# Revit family: Studio-8-Window-1
name_source: partatom
category: Windows
units: mm (PartAtom-declared; Revit-internal decimal feet)

## family parameters
Always vertical = Yes
Cut with Voids When Loaded = No
Host = Wall
OmniClass Number = 23.30.20.00
OmniClass Title = Windows
Room Calculation Point = No
Shared = No

## types (4) — shared parameters
Analytic Construction = <None>
Assembly Code = C1030
Default Sill Height = 2' - 7 1/2"
Define Thermal Properties by = Schematic Type
Description = Soundproof interior windows
Frame Finish = Clear / Dark Bronze Anodized
Frame Material = Aluminum – Studio (4/5/6/8) Soundproof Window
Glass = Laminated Glass – Studio (4/5/6/8) Soundproof Window
Height = 3' - 0"
Manufacturer = Acoustical Surfaces, Inc.
Rough Height = 3' - 0 1/2"
Type Comments = Soundproof windows
URL = https://www.acousticalsurfaces.com
Wall Closure = By host

## per-type parameters (varying)
| type | Angled | Flat | Rough Width | Width | a |
| FLAT 48 x 36 | No | Yes | 4' - 0 1/2" | 4' - 0" | 3' - 8 1/2" |
| FLAT 72 x 36 | No | Yes | 6' - 0 1/2" | 6' - 0" | 5' - 8 1/2" |
| ANGLED 72 x 36 | No | Yes | 6' - 0 1/2" | 6' - 0" | 5' - 8 1/2" |
| ANGLED 48 x 36 | Yes | No | 4' - 0 1/2" | 4' - 0" | 3' - 8 1/2" |

## geometry (parser evidence)
native form markers: Sweep x8
no freeform markers — native parametric forms only
